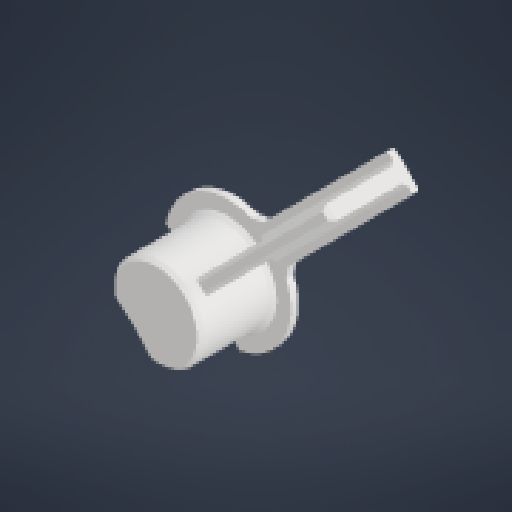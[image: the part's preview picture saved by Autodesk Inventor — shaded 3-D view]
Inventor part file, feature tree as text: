
AUTODESK INVENTOR PART (.ipt)
format: ipt  version: 2023.1 (Build 271208000, 208)  size: 451,072 bytes
history: native  units: mm
features: extrude x2, chamfer x2, sketch x2
ambient origin geometry x8: Origin, YZ Plane, XZ Plane, XY Plane, X Axis, Y Axis, Z Axis, Center Point
bodies: Body1 (feature_tree)
feature tree (6):
  extrude  "Extrusion2"  TaperAngle=45.0deg  [1 undecoded]
  extrude  "Extrusion3"  Depth=35.0mm
  chamfer  "Chamfer6"  Distance=142.0mm
  chamfer  "Chamfer7"  Angle=112.5deg  [1 undecoded]
  sketch  "Sketch3"  dims[d26=147.0mm d27=45.0deg]
  sketch  "Sketch4"  dims[d28=159.154943mm d29=35.0mm d30=142.0mm d31=112.5deg d32=157.5deg d33=5.0mm d34=5.0mm d35=1.0mm d36=2.0mm d37=0.0mm d38=25.0mm d39=2.0mm d40=2.0mm d41=5.0mm d42=20.0mm d43=0.0mm d56=3.0mm d60=1.0mm d61=2.0mm d62=45.0deg d63=2.0mm d64=2.0mm d65=45.0deg d66=187.154943mm d67=35.0mm]
note: 2 required parameter values undecoded (feature->parameter linkage not recoverable at this tier; creation-order binding heuristic only, values carry confidence <= 0.55)
